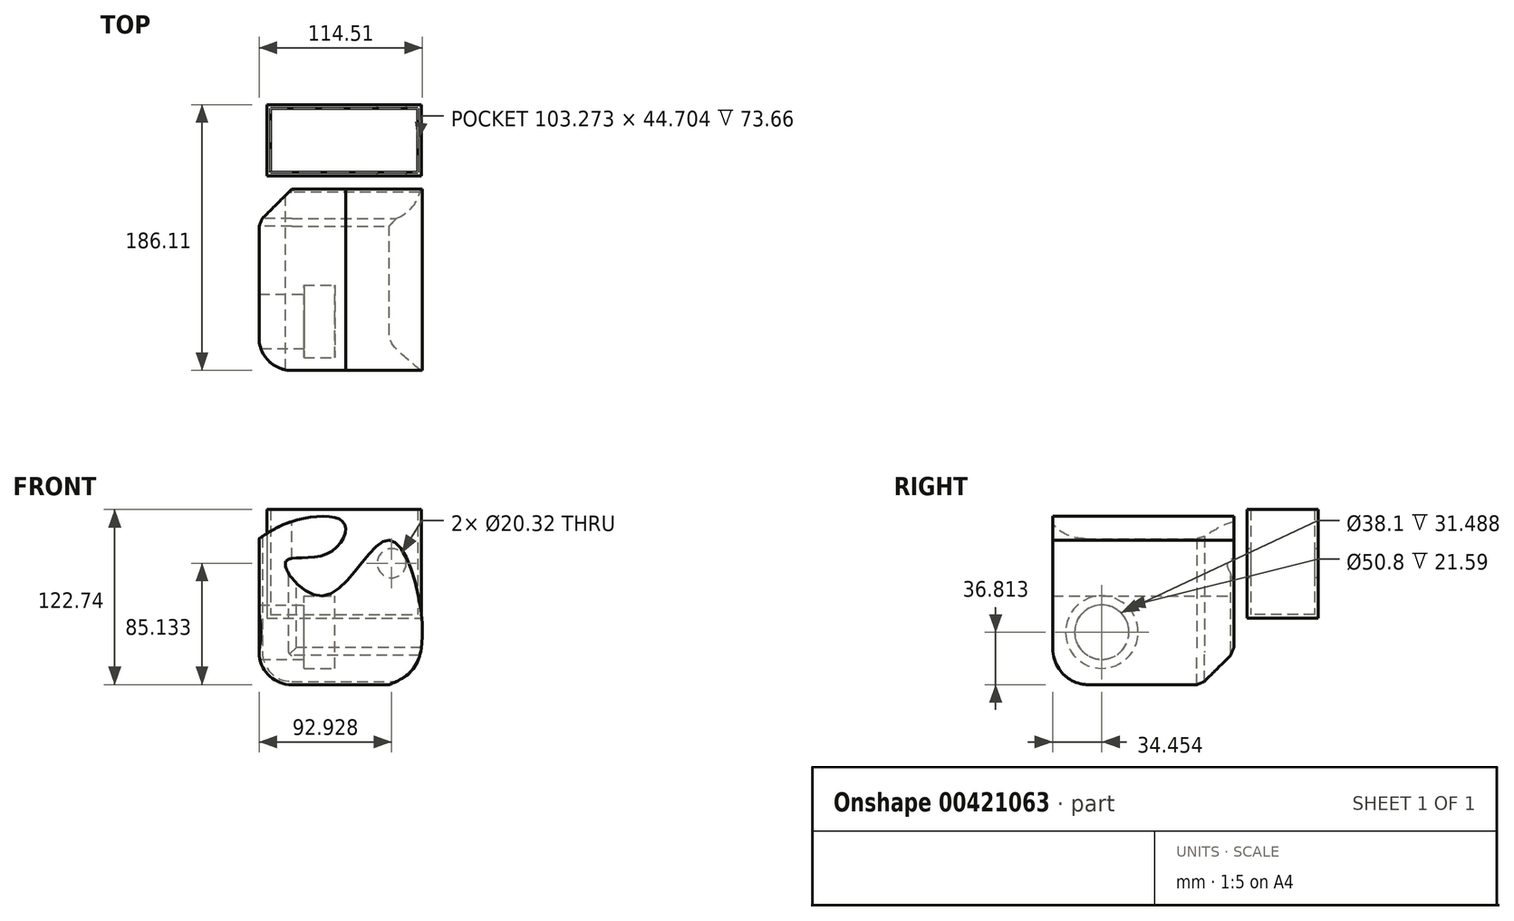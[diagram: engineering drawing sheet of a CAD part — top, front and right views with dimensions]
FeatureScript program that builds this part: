
annotation { "Feature Type Name" : "Feature", "Feature Type Description" : "" }
export const myFeature = defineFeature(function(context is Context, id is Id, definition is map)
    precondition{}
    {
        {
            var Q0;
            Q0=qCreatedBy(makeId("Front.planeOp"),FACE);
            var sketch = newSketch(context, id + "F0", { "sketchPlane" : qUnion([Q0])});
            skLineSegment(sketch, "E0", {"start": v(-53.08, 55.78) * mm, "end": v(-53.08, -46.54) * mm});
            skLineSegment(sketch, "E1", {"start": v(-53.08, -46.54) * mm, "end": v(38.05, -46.54) * mm});
            skFitSpline(sketch, "E2", {"points": [v(38.05, -46.54) * mm, v(60.43, -22.56) * mm, v(38.05, 54.82) * mm, v(-7.67, 15.81) * mm, v(-34.53, 39.15) * mm, v(-6.71, 44.6) * mm, v(6.71, 66.33) * mm, v(-25.58, 69.21) * mm, v(-53.08, 55.78) * mm], "startDerivative": vector(254.7, 110.67) * mm, "endDerivative": vector(-212.96, -141.53) * mm});
            skSolve(sketch);
        }
        {
            var Q0;
            Q0=makeQuery(id+"F0.imprint","IMPRINT",FACE,{"disambiguationData":[TD([[makeQuery(id+"F0.imprint","IMPRINT",EDGE,{"derivedFrom":sQuery(id+"F0.wireOp",EDGE,"E0")}),1.0]])]});
            extrude(context, id + "F1", {"entities" : qUnion([Q0]), "depth" : 127 * mm});
        }
        {
            var Q0;
            Q0=makeQuery(id+"F1.opExtrude","CAP_EDGE",EDGE,{"disambiguationData":[OSD([sQuery(id+"F0.wireOp",EDGE,"E1")])],"isStart":false});
            fillet(context, id + "F2", {"entities" : qUnion([Q0]), "radius" : 25.4 * mm, "tangentPropagation" : true, "allowEdgeOverflow" : false});
        }
        {
            var Q0;
            Q0=makeQuery(id+"F1.opExtrude","CAP_EDGE",EDGE,{"disambiguationData":[OSD([sQuery(id+"F0.wireOp",EDGE,"E0")])],"isStart":false});
            fillet(context, id + "F3", {"entities" : qUnion([Q0]), "radius" : 22.86 * mm, "tangentPropagation" : true, "allowEdgeOverflow" : false});
        }
        {
            var Q0;
            Q0=makeQuery(id+"F1.opExtrude","CAP_EDGE",EDGE,{"disambiguationData":[OSD([sQuery(id+"F0.wireOp",EDGE,"E1")])],"isStart":true});
            chamfer(context, id + "F4", {"entities" : qUnion([Q0]), "width" : 22.86 * mm, "tangentPropagation" : true});
        }
        {
            var Q0;
            {var subQ0=sQuery(id+"F0.wireOp",EDGE,"E1");var subQ1=sQuery(id+"F0.wireOp",EDGE,"E0");var subQ2=makeQuery(id+"F1.opExtrude","SWEPT_EDGE",EDGE,{"disambiguationData":[OSD([subQ1,subQ0])]});Q0=makeQuery(id+"F4.opChamfer","BLEND_EDGE",EDGE,{"blendedFrom":[makeQuery(id+"F3.opFillet","BLEND_EDGE",EDGE,{"blendedFrom":[subQ2,makeQuery(id+"F1.opExtrude","CAP_FACE",FACE,{"disambiguationData":[OSD([subQ1,subQ0,sQuery(id+"F0.wireOp",EDGE,"E2")])],"isStart":true})],"blendedInto":[makeQuery(id+"F1.opExtrude","CAP_FACE",FACE,{"disambiguationData":[OSD([subQ1,subQ0,sQuery(id+"F0.wireOp",EDGE,"E2")])],"isStart":true})]}),makeQuery(id+"F3.opFillet","BLEND_FACE",FACE,{"disambiguationData":[OSD([subQ1,subQ0]),TDD([subQ2])]})],"blendedInto":[makeQuery(id+"F3.opFillet","BLEND_FACE",FACE,{"disambiguationData":[OSD([subQ1,subQ0]),TDD([subQ2])]})]});}
            chamfer(context, id + "F5", {"entities" : qUnion([Q0]), "width" : 7.62 * mm, "tangentPropagation" : true});
        }
        {
            var Q0;
            {var subQ0=sQuery(id+"F0.wireOp",EDGE,"E1");Q0=makeQuery(id+"F4.opChamfer","BLEND_EDGE",EDGE,{"blendedFrom":[makeQuery(id+"F1.opExtrude","CAP_EDGE",EDGE,{"disambiguationData":[OSD([subQ0])],"isStart":true}),makeQuery(id+"F1.opExtrude","CAP_FACE",FACE,{"disambiguationData":[OSD([sQuery(id+"F0.wireOp",EDGE,"E0"),subQ0,sQuery(id+"F0.wireOp",EDGE,"E2")])],"isStart":true})],"blendedInto":[makeQuery(id+"F1.opExtrude","CAP_FACE",FACE,{"disambiguationData":[OSD([sQuery(id+"F0.wireOp",EDGE,"E0"),subQ0,sQuery(id+"F0.wireOp",EDGE,"E2")])],"isStart":true})]});}
            chamfer(context, id + "F6", {"entities" : qUnion([Q0]), "width" : 7.62 * mm, "tangentPropagation" : true});
        }
        {
            var Q0;
            Q0=qCreatedBy(makeId("Right.planeOp"),FACE);
            var sketch = newSketch(context, id + "F7", { "sketchPlane" : qUnion([Q0])});
            skPoint(sketch, "E3", {"position": v(-65.56, 6.28) * mm});
            skPoint(sketch, "E4", {"position": v(-40.46, 18.83) * mm});
            skPoint(sketch, "E5", {"position": v(-92.55, -9.73) * mm});
            skPoint(sketch, "E6", {"position": v(-48.62, -10.35) * mm});
            skPoint(sketch, "E7", {"position": v(-88.47, 32.95) * mm});
            skPoint(sketch, "E8", {"position": v(-55.84, 37.02) * mm});
            skSolve(sketch);
        }
        {
            var Q0;
            Q0=sQuery(id+"F7.wireOp",VERTEX,"E5");
            var Q1;
            Q1=makeQuery(id+"F1.opExtrude","SWEPT_BODY",BODY,{"disambiguationData":[OSD([sQuery(id+"F0.wireOp",EDGE,"E0"),sQuery(id+"F0.wireOp",EDGE,"E1"),sQuery(id+"F0.wireOp",EDGE,"E2")])]});
            hole(context, id + "F8", {"style" : HoleStyle.C_BORE, "endStyle" : HoleEndStyle.THROUGH, "holeDiameter" : 38.1 * mm, "cBoreDiameter" : 50.8 * mm, "cBoreDepth" : 21.59 * mm, "isTappedThrough" : true, "tappedDepth" : 12.7 * mm, "tapClearance" : 3, "locations" : qUnion([Q0]), "scope" : qUnion([Q1])});
        }
        {
            var Q0;
            Q0=qCreatedBy(makeId("Top.planeOp"),FACE);
            var sketch = newSketch(context, id + "F9", { "sketchPlane" : qUnion([Q0])});
            skLineSegment(sketch, "E9.bottom", {"start": v(-47.7, 59.1) * mm, "end": v(60.66, 59.1) * mm});
            skLineSegment(sketch, "E9.top", {"start": v(-47.7, 9.32) * mm, "end": v(60.66, 9.32) * mm});
            skLineSegment(sketch, "E9.left", {"start": v(-47.7, 59.1) * mm, "end": v(-47.7, 9.32) * mm});
            skLineSegment(sketch, "E9.right", {"start": v(60.66, 59.1) * mm, "end": v(60.66, 9.32) * mm});
            skSolve(sketch);
        }
        {
            var Q0;
            Q0=makeQuery(id+"F9.imprint","IMPRINT",FACE,{"disambiguationData":[TD([[makeQuery(id+"F9.imprint","IMPRINT",EDGE,{"derivedFrom":sQuery(id+"F9.wireOp",EDGE,"E9.bottom")}),-1.0]])]});
            extrude(context, id + "F10", {"entities" : qUnion([Q0]), "depth" : 76.2 * mm});
        }
        {
            var Q0;
            Q0=makeQuery(id+"F10.opExtrude","CAP_FACE",FACE,{"disambiguationData":[OSD([sQuery(id+"F9.wireOp",EDGE,"E9.bottom"),sQuery(id+"F9.wireOp",EDGE,"E9.top"),sQuery(id+"F9.wireOp",EDGE,"E9.left"),sQuery(id+"F9.wireOp",EDGE,"E9.right")])],"isStart":false});
            shell(context, id + "F11", {"entities" : qUnion([Q0]), "thickness" : 2.54 * mm});
        }
        {
            var Q0;
            Q0=qCreatedBy(makeId("Front.planeOp"),FACE);
            var sketch = newSketch(context, id + "F12", { "sketchPlane" : qUnion([Q0])});
            skPoint(sketch, "E10", {"position": v(39.85, 38.6) * mm});
            skPoint(sketch, "E11", {"position": v(15.06, 38.6) * mm});
            skPoint(sketch, "E12", {"position": v(-7.84, 38.6) * mm});
            skPoint(sketch, "E13", {"position": v(-33.26, 38.6) * mm});
            skSolve(sketch);
        }
        {
            var Q0;
            Q0=sQuery(id+"F12.wireOp",VERTEX,"E10");
            var Q1;
            Q1=makeQuery(id+"F10.opExtrude","SWEPT_BODY",BODY,{"disambiguationData":[OSD([sQuery(id+"F9.wireOp",EDGE,"E9.bottom"),sQuery(id+"F9.wireOp",EDGE,"E9.top"),sQuery(id+"F9.wireOp",EDGE,"E9.left"),sQuery(id+"F9.wireOp",EDGE,"E9.right")])]});
            hole(context, id + "F13", {"style" : HoleStyle.SIMPLE, "endStyle" : HoleEndStyle.THROUGH, "holeDiameter" : 20.32 * mm, "isTappedThrough" : true, "tappedDepth" : 12.7 * mm, "tapClearance" : 3, "locations" : qUnion([Q0]), "scope" : qUnion([Q1])});
        }
    });
